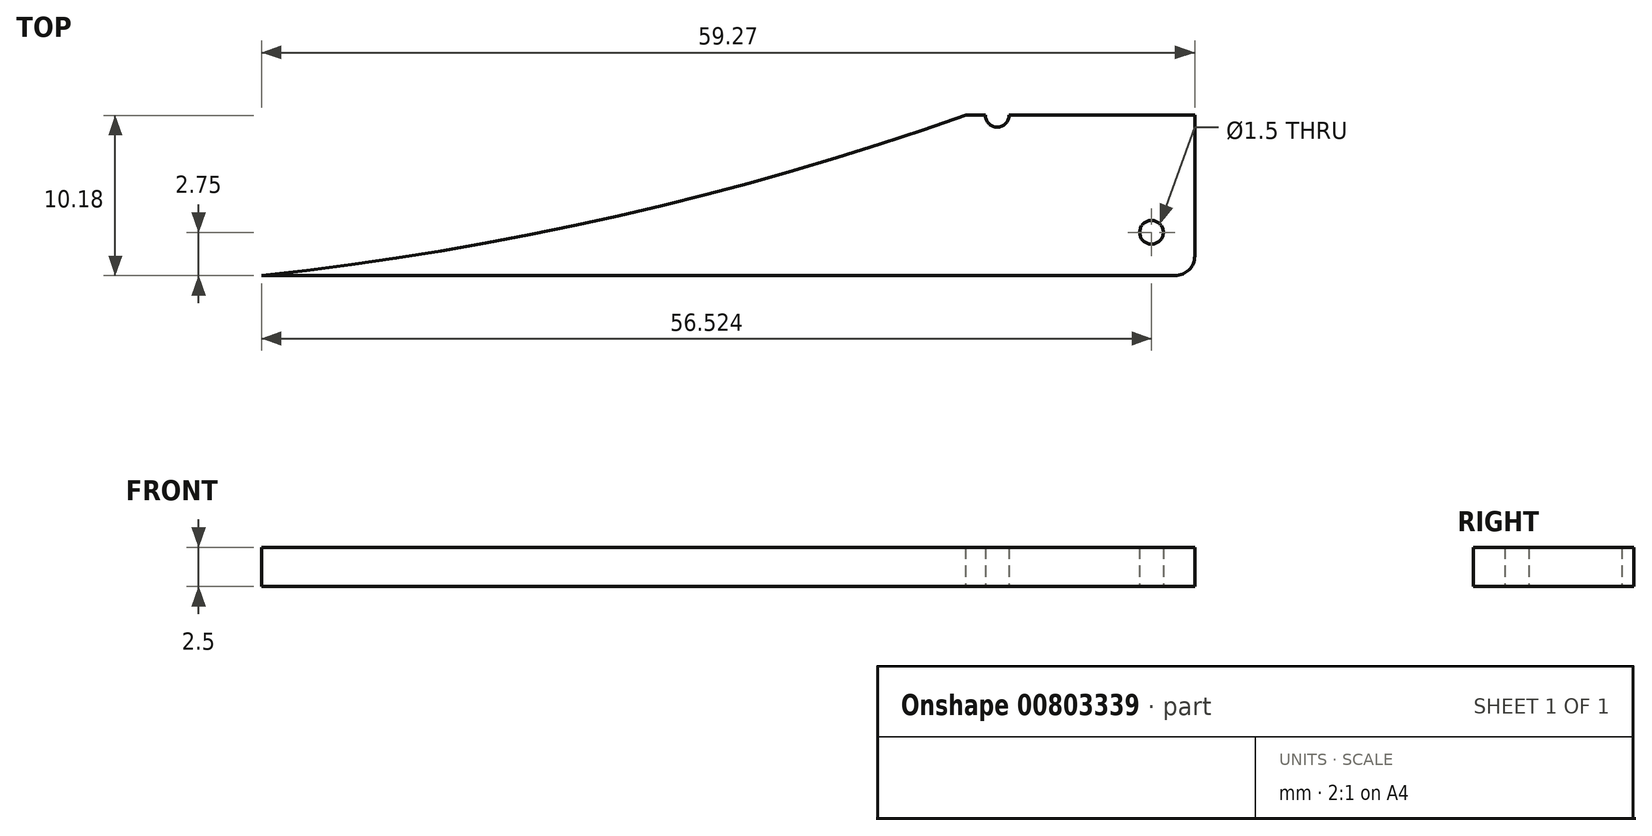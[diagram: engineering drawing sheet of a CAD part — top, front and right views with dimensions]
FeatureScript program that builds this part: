
annotation { "Feature Type Name" : "Feature", "Feature Type Description" : "" }
export const myFeature = defineFeature(function(context is Context, id is Id, definition is map)
    precondition{}
    {
        {
            var Q0;
            Q0=qCreatedBy(makeId("Top.planeOp"),FACE);
            var sketch = newSketch(context, id + "F0", { "sketchPlane" : qUnion([Q0])});
            skLineSegment(sketch, "E0.bottom", {"start": v(0, 0) * mm, "end": v(58.02, 0) * mm});
            skLineSegment(sketch, "E0.right", {"start": v(59.27, 1.25) * mm, "end": v(59.27, 10.18) * mm});
            skArc(sketch, "E1", {"start": v(0, 0) * mm, "mid": v(22.66, 3.8) * mm, "end": v(44.73, 10.18) * mm});
            skLineSegment(sketch, "E2.bottom", {"start": v(44.73, 10.18) * mm, "end": v(45.98, 10.18) * mm});
            skPoint(sketch, "E2.right.end.orphan", {"position": v(59.27, 7.5) * mm});
            skPoint(sketch, "E3.orphan", {"position": v(59.27, 15) * mm});
            skArc(sketch, "E4", {"start": v(58.02, 0) * mm, "mid": v(58.9, 0.37) * mm, "end": v(59.27, 1.25) * mm});
            skPoint(sketch, "E5.orphan", {"position": v(59.27, 0) * mm});
            skArc(sketch, "E6", {"start": v(45.98, 10.18) * mm, "mid": v(46.73, 9.43) * mm, "end": v(47.48, 10.18) * mm});
            skLineSegment(sketch, "E7.trimOffspring", {"start": v(47.48, 10.18) * mm, "end": v(53.77, 10.18) * mm});
            skCircle(sketch, "E8", {"center": v(56.52, 2.75) * mm, "radius": 0.75 * mm});
            skLineSegment(sketch, "E9.bottom", {"start": v(53.77, 10.18) * mm, "end": v(59.27, 10.18) * mm});
            skPoint(sketch, "E10.center.orphan", {"position": v(53.77, 10.68) * mm});
            skPoint(sketch, "E11.center.orphan", {"position": v(56.77, 13) * mm});
            skPoint(sketch, "E12.center.orphan", {"position": v(54.77, 14.5) * mm});
            skSolve(sketch);
        }
        {
            var Q0;
            Q0 = qSketchRegion(id + "F0", true);
            extrude(context, id + "F1", {"entities" : qUnion([Q0]), "depth" : 2.5 * mm, "offsetDistance" : 25 * mm});
        }
    });
